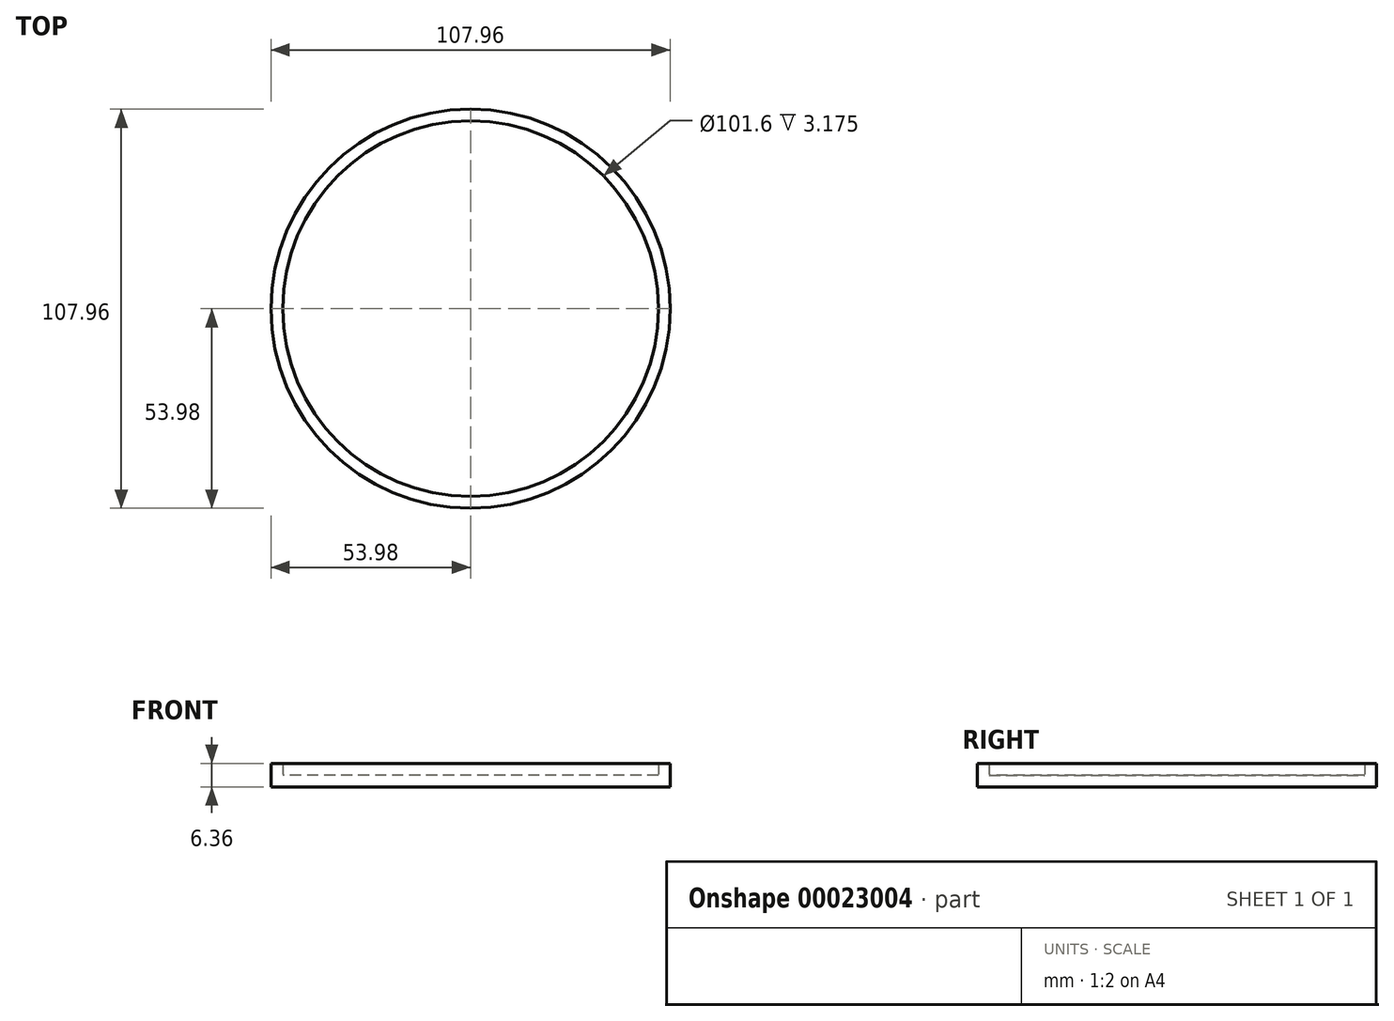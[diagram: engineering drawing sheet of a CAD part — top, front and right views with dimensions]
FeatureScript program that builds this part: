
annotation { "Feature Type Name" : "Feature", "Feature Type Description" : "" }
export const myFeature = defineFeature(function(context is Context, id is Id, definition is map)
    precondition{}
    {
        {
            var Q0;
            Q0=qCreatedBy(makeId("Top.planeOp"),FACE);
            var sketch = newSketch(context, id + "F0", { "sketchPlane" : qUnion([Q0])});
            skCircle(sketch, "E0", {"center": v(0, 0) * mm, "radius": 50.8 * mm});
            skCircle(sketch, "E1", {"center": v(0, 0) * mm, "radius": 53.97 * mm});
            skSolve(sketch);
        }
        {
            var Q0;
            Q0=makeQuery(id+"F0.imprint","IMPRINT",FACE,{"disambiguationData":[TD([[makeQuery(id+"F0.imprint","IMPRINT",EDGE,{"derivedFrom":sQuery(id+"F0.wireOp",EDGE,"E0")}),-1.0]])]});
            extrude(context, id + "F1", {"entities" : qUnion([Q0]), "depth" : 3.17 * mm});
        }
        {
            var Q0;
            Q0=makeQuery(id+"F1.opExtrude","CAP_FACE",FACE,{"disambiguationData":[OSD([sQuery(id+"F0.wireOp",EDGE,"E0"),sQuery(id+"F0.wireOp",EDGE,"E1")])],"isStart":true});
            var sketch = newSketch(context, id + "F2", { "sketchPlane" : qUnion([Q0])});
            skCircle(sketch, "E2.0", {"center": v(0, 0) * mm, "radius": 53.97 * mm});
            skSolve(sketch);
        }
        {
            var Q0;
            Q0 = qSketchRegion(id + "F2", true);
            extrude(context, id + "F3", {"entities" : qUnion([Q0]), "operationType" : NewBodyOperationType.ADD, "depth" : 3.17 * mm});
        }
    });
